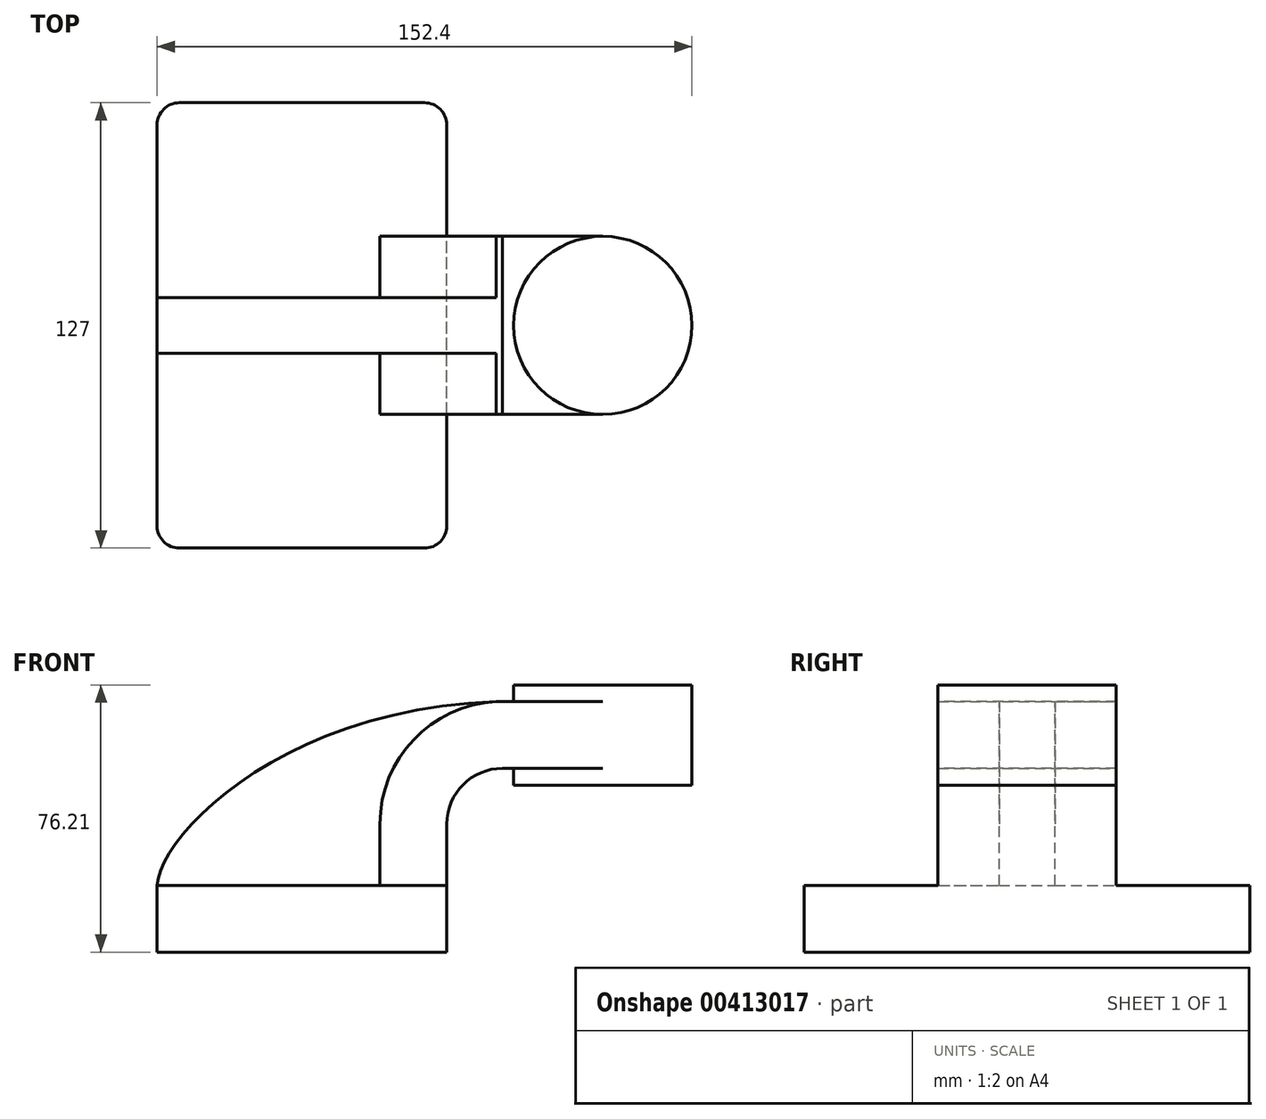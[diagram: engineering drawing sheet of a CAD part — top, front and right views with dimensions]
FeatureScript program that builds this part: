
annotation { "Feature Type Name" : "Feature", "Feature Type Description" : "" }
export const myFeature = defineFeature(function(context is Context, id is Id, definition is map)
    precondition{}
    {
        {
            var Q0;
            Q0=qCreatedBy(makeId("Front.planeOp"),FACE);
            var sketch = newSketch(context, id + "F0", { "sketchPlane" : qUnion([Q0])});
            skLineSegment(sketch, "E0.bottom", {"start": v(27.5, -9.53) * mm, "end": v(-55.06, -9.52) * mm});
            skLineSegment(sketch, "E0.top", {"start": v(27.5, 9.53) * mm, "end": v(-55.06, 9.53) * mm});
            skLineSegment(sketch, "E0.left", {"start": v(27.5, -9.53) * mm, "end": v(27.5, 9.52) * mm});
            skLineSegment(sketch, "E0.right", {"start": v(-55.06, -9.53) * mm, "end": v(-55.06, 9.52) * mm});
            skPoint(sketch, "E0.middle", {"position": v(-13.78, 0) * mm});
            skLineSegment(sketch, "E1.bottom", {"start": v(97.34, 38.1) * mm, "end": v(46.54, 38.1) * mm});
            skLineSegment(sketch, "E1.top", {"start": v(97.34, 66.67) * mm, "end": v(46.54, 66.67) * mm});
            skLineSegment(sketch, "E1.left", {"start": v(97.34, 38.1) * mm, "end": v(97.34, 66.67) * mm});
            skLineSegment(sketch, "E1.right", {"start": v(46.54, 38.1) * mm, "end": v(46.54, 66.67) * mm});
            skPoint(sketch, "E1.middle", {"position": v(71.94, 52.39) * mm});
            skLineSegment(sketch, "E2", {"start": v(27.5, 9.52) * mm, "end": v(27.5, 27) * mm});
            skArc(sketch, "E3", {"start": v(27.5, 27) * mm, "mid": v(32.14, 38.23) * mm, "end": v(43.37, 42.88) * mm});
            skLineSegment(sketch, "E4", {"start": v(43.37, 42.88) * mm, "end": v(71.94, 42.88) * mm});
            skLineSegment(sketch, "E5.0", {"start": v(43.37, 61.93) * mm, "end": v(71.94, 61.93) * mm});
            skArc(sketch, "E5.1", {"start": v(8.44, 27) * mm, "mid": v(18.67, 51.7) * mm, "end": v(43.37, 61.93) * mm});
            skLineSegment(sketch, "E5.2", {"start": v(8.44, 9.52) * mm, "end": v(8.44, 27) * mm});
            skLineSegment(sketch, "E6", {"start": v(71.94, 66.67) * mm, "end": v(71.94, 38.1) * mm});
            skFitSpline(sketch, "E7", {"points": [v(-55.06, 9.53) * mm, v(43.37, 61.93) * mm], "startDerivative": vector(2.3, 42.57) * mm, "endDerivative": vector(187.09, 3.85) * mm});
            skSolve(sketch);
        }
        {
            var Q0;
            Q0=makeQuery(id+"F0.imprint","IMPRINT",FACE,{"disambiguationData":[TD([[makeQuery(id+"F0.imprint","IMPRINT",EDGE,{"derivedFrom":sQuery(id+"F0.wireOp",EDGE,"E0.bottom")}),-1.0]])]});
            extrude(context, id + "F1", {"entities" : qUnion([Q0]), "endBound" : BoundingType.SYMMETRIC, "depth" : 127 * mm});
        }
        {
            var Q0;
            {var subQ3=sQuery(id+"F0.wireOp",EDGE,"E5.2");Q0=makeQuery(id+"F0.imprint","IMPRINT",FACE,{"disambiguationData":[TD([[makeQuery(id+"F0.imprint","IMPRINT",EDGE,{"derivedFrom":subQ3}),1.0]])]});}
            extrude(context, id + "F2", {"entities" : qUnion([Q0]), "operationType" : NewBodyOperationType.ADD, "endBound" : BoundingType.SYMMETRIC, "depth" : 15.88 * mm});
        }
        {
            var Q0;
            {var subQ1=sQuery(id+"F0.wireOp",EDGE,"E2");Q0=makeQuery(id+"F0.imprint","IMPRINT",FACE,{"disambiguationData":[TD([[makeQuery(id+"F0.imprint","IMPRINT",EDGE,{"derivedFrom":subQ1}),1.0]])]});}
            var Q1;
            {var subQ0=sQuery(id+"F0.wireOp",EDGE,"E4");var subQ1=sQuery(id+"F0.wireOp",EDGE,"E1.right");var subQ2=makeQuery(id+"F0.imprint","INTERSECT",VERTEX,{"derivedFrom":[subQ1,subQ0]});Q1=makeQuery(id+"F0.imprint","IMPRINT",FACE,{"disambiguationData":[TD([[makeQuery(id+"F0.imprint","IMPRINT",EDGE,{"disambiguationData":[TD([[subQ2,-1.0]])],"derivedFrom":subQ1}),-1.0]])]});}
            extrude(context, id + "F3", {"entities" : qUnion([Q0, Q1]), "operationType" : NewBodyOperationType.ADD, "endBound" : BoundingType.SYMMETRIC, "depth" : 50.8 * mm});
        }
        {
            var Q0;
            {var subQ0=sQuery(id+"F0.wireOp",EDGE,"E1.left");Q0=makeQuery(id+"F0.imprint","IMPRINT",FACE,{"disambiguationData":[TD([[makeQuery(id+"F0.imprint","IMPRINT",EDGE,{"derivedFrom":subQ0}),1.0]])]});}
            var Q1;
            Q1=sQuery(id+"F0.wireOp",EDGE,"E6");
            revolve(context, id + "F4", {"operationType" : NewBodyOperationType.ADD, "entities" : qUnion([Q0]), "axis" : qUnion([Q1]), "revolveType" : RevolveType.FULL});
        }
        {
            var Q0;
            Q0=makeQuery(id+"F1.opExtrude","CAP_EDGE",EDGE,{"disambiguationData":[OSD([sQuery(id+"F0.wireOp",EDGE,"E0.right")])],"isStart":false});
            var Q1;
            Q1=makeQuery(id+"F1.opExtrude","CAP_EDGE",EDGE,{"disambiguationData":[OSD([sQuery(id+"F0.wireOp",EDGE,"E0.left")])],"isStart":false});
            var Q2;
            Q2=makeQuery(id+"F1.opExtrude","CAP_EDGE",EDGE,{"disambiguationData":[OSD([sQuery(id+"F0.wireOp",EDGE,"E0.right")])],"isStart":true});
            var Q3;
            Q3=makeQuery(id+"F1.opExtrude","CAP_EDGE",EDGE,{"disambiguationData":[OSD([sQuery(id+"F0.wireOp",EDGE,"E0.left")])],"isStart":true});
            fillet(context, id + "F5", {"entities" : qUnion([Q0, Q1, Q2, Q3]), "radius" : 6.35 * mm, "tangentPropagation" : true, "allowEdgeOverflow" : false});
        }
    });
